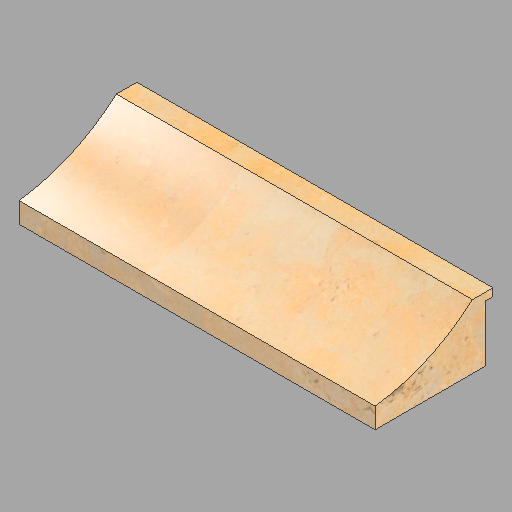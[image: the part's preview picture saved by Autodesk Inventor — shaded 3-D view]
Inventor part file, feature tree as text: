
AUTODESK INVENTOR PART (.ipt)
format: ipt  version: 2022.2 (Build 262287010, 287A)  size: 276,992 bytes
history: native  units: in
note: dims shown in document units (in); Inventor stores cm internally (conversion verified against a paired STEP export)
features: revolve x2, direct_edit x1, other x1
ambient origin geometry x8: Origin, YZ Plane, XZ Plane, XY Plane, X Axis, Y Axis, Z Axis, Center Point
bodies: Solid1 (feature_tree)
feature tree (4):
  direct_edit  "Direct Edit1"
  other  "Head (R) (1)"
  revolve  "Rotate1"  [1 undecoded]
  revolve  "Rotate2"  [1 undecoded]
note: 2 required parameter values undecoded (feature->parameter linkage not recoverable at this tier; creation-order binding heuristic only, values carry confidence <= 0.55)
